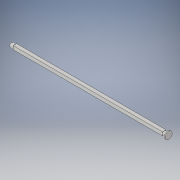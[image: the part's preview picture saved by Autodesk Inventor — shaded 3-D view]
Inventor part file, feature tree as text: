
AUTODESK INVENTOR PART (.ipt)
format: ipt  version: 2017 (Build 210142000, 142)  size: 126,464 bytes
history: native  units: in
note: dims shown in document units (in); Inventor stores cm internally (conversion verified against a paired STEP export)
features: extrude x4, sketch x4
ambient origin geometry x8: Origin, YZ Plane, XZ Plane, XY Plane, X Axis, Y Axis, Z Axis, Center Point
bodies: Solid1 (feature_tree)
feature tree (8):
  extrude  "Extrusion1"  Depth=0.25in
  extrude  "Extrusion2"  TaperAngle=0.0deg  [1 undecoded]
  extrude  "Extrusion3"  Depth=0.125in
  extrude  "Extrusion4"  Depth=0.25in
  sketch  "Sketch1"  dims[d0=10.614in d1=0.25in]
  sketch  "Sketch2"  dims[d2=0.25in d3=0.0in]
  sketch  "Sketch3"  dims[d4=0.125in d5=0.125in]
  sketch  "Sketch4"  dims[d6=0.25in d7=0.25in d8=0.0in d9=0.125in d10=0.125in d11=0.25in d12=0.25in d13=0.0in d14=0.5in d15=0.0625in d16=0.0in]
note: 1 required parameter value undecoded (feature->parameter linkage not recoverable at this tier; creation-order binding heuristic only, values carry confidence <= 0.55)
